# Revit family: Festpunkt Typ AK-MD, T-Stahl
name_source: partatom
category: HLS-Bauteile
revit_build: Autodesk Revit 2017 (Build: 20190507_1515(x64)
units: mm (PartAtom-declared; Revit-internal decimal feet)

## family parameters
Arbeitsebenenbasiert = Ja
Beim Laden mit Abzugskörper schneiden = Nein
Bemaßung runder Anschluss = Durchmesser verwenden
Gemeinsam genutzt = Ja
Immer vertikal = Nein
Raumberechnungspunkt = Nein
Teiletyp = Normal

## types (7) — shared parameters
Anzahl Rohrschellen = 6
Aufbaumaß = 56 mm
Ausführung = mit Klemmschelle
Breite Material Rohrschelle = 25 mm
Druckstück Typ I = Druckstück Typ I Gummi
Fabrikat = MEFA
Firma = MEFA Befestigungs- und Montagesysteme GmbH
Kurztext1 = Festpunkt Typ A/K-MD
Länge Profilstahl = 100 mm  [stored 0.328084 ft]
Länge Schweißnase = 81 mm
Mengeneinheit = St
Profilstahltyp = T30
Rohrschellentyp = Maxima PSM
Schalldämmeinlage = Gummi
Stärke Material Rohrschelle = 3 mm
Vorgabe-Ansicht = 1219 mm
max. Temperaturbeständigkeit = 100 °C
vpe = 1 St
zero-valued in all types: Rohraußendurchmesser

## per-type parameters (varying)
| type | Artikelnummer | Breite | EAN | Gewicht | Gewicht pro Bauteil | Höhe 1 | Höhe 2 | Kurztext2 | RA | Rohrschellen Maxima | max. Axiale Reaktionskraft |
| Festpunkt Typ AK-MD, T-Stahl, Ø 15- 19, Gummi | 0020155 | 80 mm  [stored 0.262467 ft] | 4250928400055 | 1.58 kg | 1.58 kg | 61 mm | 65 mm | 15 - 19 mm Gummi mit Klemmschelle | 48 mm  [stored 0.15748 ft] | MEFA RS Maxima PSM, Ø15-Ø57 mm, TPE : MEFA RS Maxima PSM, Ø15-Ø19 mm, TPE | 2 kN |
| Festpunkt Typ AK-MD, T-Stahl, Ø 20- 25, Gummi | 0020215 | 87 mm  [stored 0.285433 ft] | 4250928400093 | 1.65 kg | 1.65 kg | 66 mm | 71 mm | 20 - 25 mm Gummi mit Klemmschelle | 51 mm | MEFA RS Maxima PSM, Ø15-Ø57 mm, TPE : MEFA RS Maxima PSM, Ø20-Ø25 mm, TPE |  |
| Festpunkt Typ AK-MD, T-Stahl, Ø 26- 30, Gummi | 0020265 | 92 mm  [stored 0.301837 ft] | 4250928400147 | 1.74 kg | 1.74 kg | 72 mm | 76 mm | 26 - 30 mm Gummi mit Klemmschelle | 53 mm  [stored 0.173885 ft] | MEFA RS Maxima PSM, Ø15-Ø57 mm, TPE : MEFA RS Maxima PSM, Ø26-Ø30 mm, TPE |  |
| Festpunkt Typ AK-MD, T-Stahl, Ø 31- 36, Gummi | 0020315 | 98 mm  [stored 0.321522 ft] | 4250928400192 | 1.81 kg | 1.81 kg | 77 mm | 82 mm | 31 - 36 mm Gummi mit Klemmschelle | 56 mm  [stored 0.183727 ft] | MEFA RS Maxima PSM, Ø15-Ø57 mm, TPE : MEFA RS Maxima PSM, Ø31-Ø36 mm, TPE |  |
| Festpunkt Typ AK-MD, T-Stahl, Ø 38- 45, Gummi | 0020385 | 107 mm  [stored 0.35105 ft] | 4250928400239 | 1.92 kg | 1.92 kg | 84 mm | 91 mm | 38 - 45 mm Gummi mit Klemmschelle | 61 mm  [stored 0.200131 ft] | MEFA RS Maxima PSM, Ø15-Ø57 mm, TPE : MEFA RS Maxima PSM, Ø38-Ø45 mm, TPE |  |
| Festpunkt Typ AK-MD, T-Stahl, Ø 47- 51, Gummi | 0020475 | 114 mm  [stored 0.374016 ft] | 4250928400284 | 2.05 kg | 2.05 kg | 93 mm | 97 mm | 47 - 51 mm Gummi mit Klemmschelle | 64 mm  [stored 0.209974 ft] | MEFA RS Maxima PSM, Ø15-Ø57 mm, TPE : MEFA RS Maxima PSM, Ø47-Ø51 mm, TPE |  |
| Festpunkt Typ AK-MD, T-Stahl, Ø 53- 57, Gummi | 0020535 | 120 mm  [stored 0.393701 ft] | 4250928400321 | 2.14 kg | 2.14 kg | 99 mm | 103 mm | 53 - 57 mm Gummi mit Klemmschelle | 67 mm | MEFA RS Maxima PSM, Ø15-Ø57 mm, TPE : MEFA RS Maxima PSM, Ø53-Ø57 mm, TPE |  |

note: [stored X ft] marks values corroborated as IEEE doubles in the binary element streams (Revit-internal decimal feet)

## geometry (parser evidence)
native form markers: Sweep x3
no freeform markers — native parametric forms only
